# Revit family: 873-00-002-DN700-800
name_source: partatom
category: Pipe Accessories
units: mm (PartAtom-declared; Revit-internal decimal feet)

## family parameters
Always vertical = Yes
Cut with Voids When Loaded = No
Part Type = Valve - Breaks Into
Round Connector Dimension = Use Diameter
Shared = No
Work Plane-Based = No

## types (2) — shared parameters
873-0700-00-741000 = DN700_PN25
873-0800-00-741000 = DN800_PN25
Angle = 22.50°
Body_Wallthicknss = 10 mm  [stored 0.0328084 ft]
Description_ = AVK DISMANTLING JOINT
Flange_thickness = 20 mm  [stored 0.0656168 ft]
Search_table = 873-00-002-DN700-800
URL product pages = https://www.avkvalves.com

## per-type parameters (varying)
| type | A | DN | Id(Radius) | L | T | d1 | d2 |
| DN700 | 315 mm  [stored 1.03346 ft] | 700 mm  [stored 2.29659 ft] | 350 mm  [stored 1.14829 ft] | 550 mm  [stored 1.80446 ft] | 39 mm  [stored 0.127953 ft] | 875 mm  [stored 2.87073 ft] | 480 mm  [stored 1.5748 ft] |
| DN800 | 335 mm  [stored 1.09908 ft] | 800 mm  [stored 2.62467 ft] | 400 mm  [stored 1.31234 ft] | 620 mm  [stored 2.03412 ft] | 45 mm  [stored 0.147638 ft] | 990 mm  [stored 3.24803 ft] | 543 mm |

note: [stored X ft] marks values corroborated as IEEE doubles in the binary element streams (Revit-internal decimal feet)

## geometry (parser evidence)
native form markers: Sweep x4
no freeform markers — native parametric forms only
